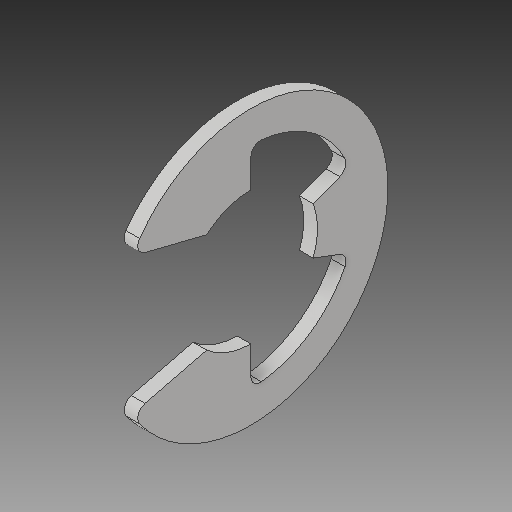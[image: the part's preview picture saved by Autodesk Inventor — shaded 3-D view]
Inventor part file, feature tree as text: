
AUTODESK INVENTOR PART (.ipt)
format: ipt  version: 2018 (Build 220112000, 112)  size: 105,472 bytes
history: native  units: in
note: dims shown in document units (in); Inventor stores cm internally (conversion verified against a paired STEP export)
features: fillet x1
ambient origin geometry x8: Origin, YZ Plane, XZ Plane, XY Plane, X Axis, Y Axis, Z Axis, Center Point
bodies: Solid1 (feature_tree)
feature tree (1):
  fillet  "Fillet1"  [1 undecoded]
note: 1 required parameter value undecoded (feature->parameter linkage not recoverable at this tier; creation-order binding heuristic only, values carry confidence <= 0.55)
